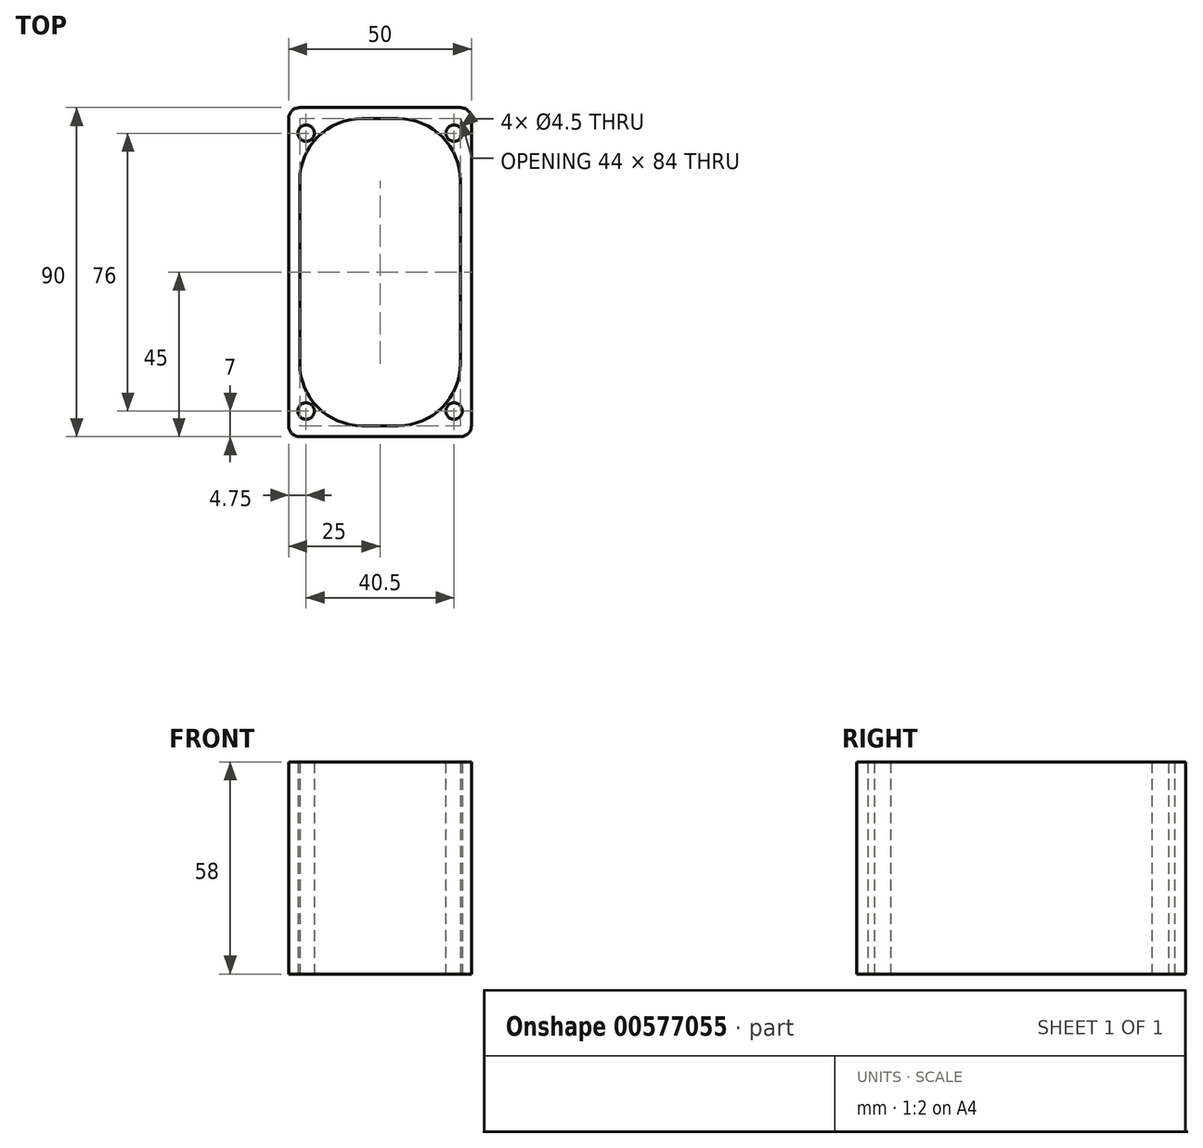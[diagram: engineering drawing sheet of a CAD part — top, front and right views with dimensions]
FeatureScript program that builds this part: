
annotation { "Feature Type Name" : "Feature", "Feature Type Description" : "" }
export const myFeature = defineFeature(function(context is Context, id is Id, definition is map)
    precondition{}
    {
        {
            var Q0;
            Q0=qCreatedBy(makeId("Top.planeOp"),FACE);
            var sketch = newSketch(context, id + "F0", { "sketchPlane" : qUnion([Q0])});
            skLineSegment(sketch, "E0.bottom", {"start": v(22, -45) * mm, "end": v(-22, -45) * mm});
            skLineSegment(sketch, "E0.top", {"start": v(22, 45) * mm, "end": v(-22, 45) * mm});
            skLineSegment(sketch, "E0.left", {"start": v(25, -42) * mm, "end": v(25, 42) * mm});
            skLineSegment(sketch, "E0.right", {"start": v(-25, -42) * mm, "end": v(-25, 42) * mm});
            skPoint(sketch, "E0.middle", {"position": v(0, 0) * mm});
            skLineSegment(sketch, "E1.bottom", {"start": v(5, -42) * mm, "end": v(-5, -42) * mm});
            skLineSegment(sketch, "E1.top", {"start": v(5, 42) * mm, "end": v(-5, 42) * mm});
            skLineSegment(sketch, "E1.left", {"start": v(22, -25) * mm, "end": v(22, 25) * mm});
            skLineSegment(sketch, "E1.right", {"start": v(-22, -25) * mm, "end": v(-22, 25) * mm});
            skPoint(sketch, "E2.visualSharp", {"position": v(-22, 42) * mm});
            skArc(sketch, "E2.filletArc", {"start": v(-5, 42) * mm, "mid": v(-17.02, 37.02) * mm, "end": v(-22, 25) * mm});
            skPoint(sketch, "E3.visualSharp", {"position": v(22, 42) * mm});
            skArc(sketch, "E3.filletArc", {"start": v(22, 25) * mm, "mid": v(17.02, 37.02) * mm, "end": v(5, 42) * mm});
            skPoint(sketch, "E4.visualSharp", {"position": v(-22, -42) * mm});
            skArc(sketch, "E4.filletArc", {"start": v(-22, -25) * mm, "mid": v(-17.02, -37.02) * mm, "end": v(-5, -42) * mm});
            skPoint(sketch, "E5.visualSharp", {"position": v(22, -42) * mm});
            skArc(sketch, "E5.filletArc", {"start": v(5, -42) * mm, "mid": v(17.02, -37.02) * mm, "end": v(22, -25) * mm});
            skLineSegment(sketch, "E6.bottom", {"start": v(20.25, -38) * mm, "end": v(-20.25, -38) * mm, "construction": true});
            skLineSegment(sketch, "E6.top", {"start": v(20.25, 38) * mm, "end": v(-20.25, 38) * mm, "construction": true});
            skLineSegment(sketch, "E6.left", {"start": v(20.25, -38) * mm, "end": v(20.25, 38) * mm, "construction": true});
            skLineSegment(sketch, "E6.right", {"start": v(-20.25, -38) * mm, "end": v(-20.25, 38) * mm, "construction": true});
            skCircle(sketch, "E7", {"center": v(20.25, 38) * mm, "radius": 2.25 * mm});
            skCircle(sketch, "E8.MirrorC", {"center": v(-20.25, 38) * mm, "radius": 2.25 * mm});
            skCircle(sketch, "E9.MirrorC", {"center": v(20.25, -38) * mm, "radius": 2.25 * mm});
            skCircle(sketch, "E10.MirrorC", {"center": v(-20.25, -38) * mm, "radius": 2.25 * mm});
            skPoint(sketch, "E11.visualSharp", {"position": v(-25, 45) * mm});
            skArc(sketch, "E11.filletArc", {"start": v(-22, 45) * mm, "mid": v(-24.12, 44.12) * mm, "end": v(-25, 42) * mm});
            skPoint(sketch, "E12.visualSharp", {"position": v(25, 45) * mm});
            skArc(sketch, "E12.filletArc", {"start": v(25, 42) * mm, "mid": v(24.12, 44.12) * mm, "end": v(22, 45) * mm});
            skPoint(sketch, "E13.visualSharp", {"position": v(-25, -45) * mm});
            skArc(sketch, "E13.filletArc", {"start": v(-25, -42) * mm, "mid": v(-24.12, -44.12) * mm, "end": v(-22, -45) * mm});
            skPoint(sketch, "E14.visualSharp", {"position": v(25, -45) * mm});
            skArc(sketch, "E14.filletArc", {"start": v(22, -45) * mm, "mid": v(24.12, -44.12) * mm, "end": v(25, -42) * mm});
            skSolve(sketch);
        }
        {
            var Q0;
            Q0=makeQuery(id+"F0.imprint","IMPRINT",FACE,{"disambiguationData":[TD([[makeQuery(id+"F0.imprint","IMPRINT",EDGE,{"derivedFrom":sQuery(id+"F0.wireOp",EDGE,"E0.bottom")}),-1.0]])]});
            extrude(context, id + "F1", {"entities" : qUnion([Q0]), "depth" : 58 * mm, "offsetDistance" : 25 * mm});
        }
    });
